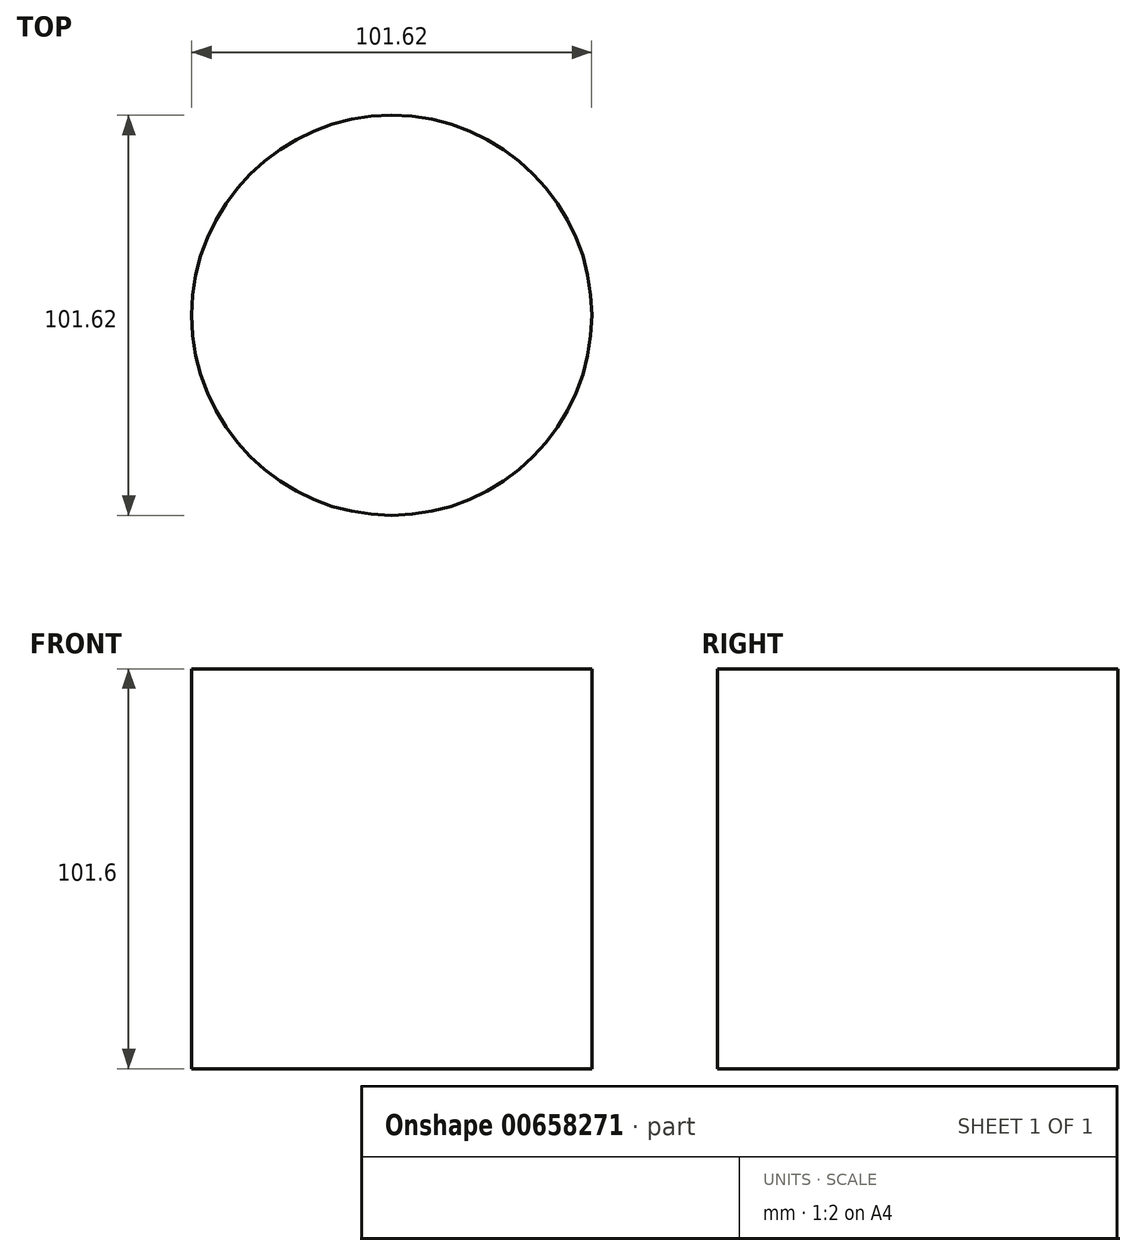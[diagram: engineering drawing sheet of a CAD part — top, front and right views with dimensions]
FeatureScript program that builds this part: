
annotation { "Feature Type Name" : "Feature", "Feature Type Description" : "" }
export const myFeature = defineFeature(function(context is Context, id is Id, definition is map)
    precondition{}
    {
        {
            var Q0;
            Q0=qCreatedBy(makeId("Top.planeOp"),FACE);
            var sketch = newSketch(context, id + "F0", { "sketchPlane" : qUnion([Q0])});
            skCircle(sketch, "E0", {"center": v(0, 0) * mm, "radius": 50.81 * mm});
            skSolve(sketch);
        }
        {
            var Q0;
            Q0=makeQuery(id+"F0.imprint","IMPRINT",FACE,{"disambiguationData":[TD([[makeQuery(id+"F0.imprint","IMPRINT",EDGE,{"derivedFrom":sQuery(id+"F0.wireOp",EDGE,"E0")}),1.0]])]});
            extrude(context, id + "F1", {"entities" : qUnion([Q0]), "depth" : 101.6 * mm, "offsetDistance" : 25.4 * mm});
        }
    });
